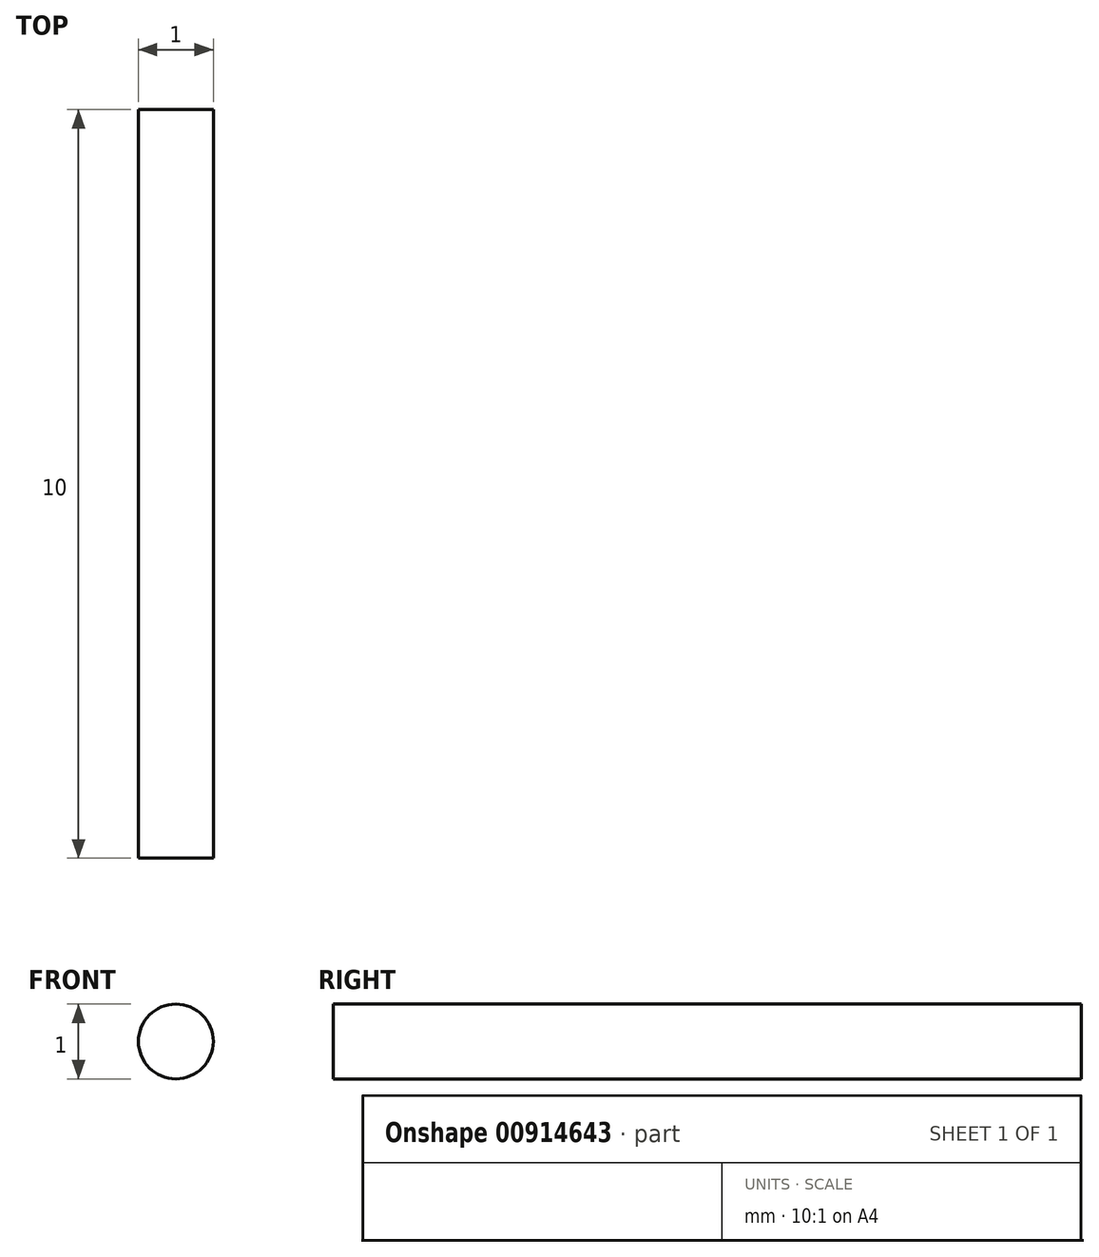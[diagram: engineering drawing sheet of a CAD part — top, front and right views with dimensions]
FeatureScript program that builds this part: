
annotation { "Feature Type Name" : "Feature", "Feature Type Description" : "" }
export const myFeature = defineFeature(function(context is Context, id is Id, definition is map)
    precondition{}
    {
        {
            var Q0;
            Q0=qCreatedBy(makeId("Front.planeOp"),FACE);
            var sketch = newSketch(context, id + "F0", { "sketchPlane" : qUnion([Q0])});
            skCircle(sketch, "E0", {"center": v(0, 0) * mm, "radius": 0.5 * mm});
            skSolve(sketch);
        }
        {
            var Q0;
            Q0=qSketchRegion(id+"F0",true);
            extrude(context, id + "F1", {"entities" : qUnion([Q0]), "depth" : 10 * mm, "offsetDistance" : 25 * mm});
        }
    });
